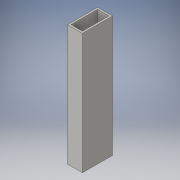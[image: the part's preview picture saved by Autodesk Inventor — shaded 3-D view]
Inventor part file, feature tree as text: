
AUTODESK INVENTOR PART (.ipt)
format: ipt  version: 2016 (Build 200138000, 138)  size: 92,672 bytes
history: native  units: in
note: dims shown in document units (in); Inventor stores cm internally (conversion verified against a paired STEP export)
features: extrude x1, sketch x1
ambient origin geometry x8: Origin, YZ Plane, XZ Plane, XY Plane, X Axis, Y Axis, Z Axis, Center Point
bodies: Solid1 (feature_tree)
feature tree (2):
  extrude  "Extrusion1"  Depth=2.0in
  sketch  "Sketch1"  dims[d0=1.0in d1=2.0in d2=0.125in d3=8.0in d4=0.0in]
